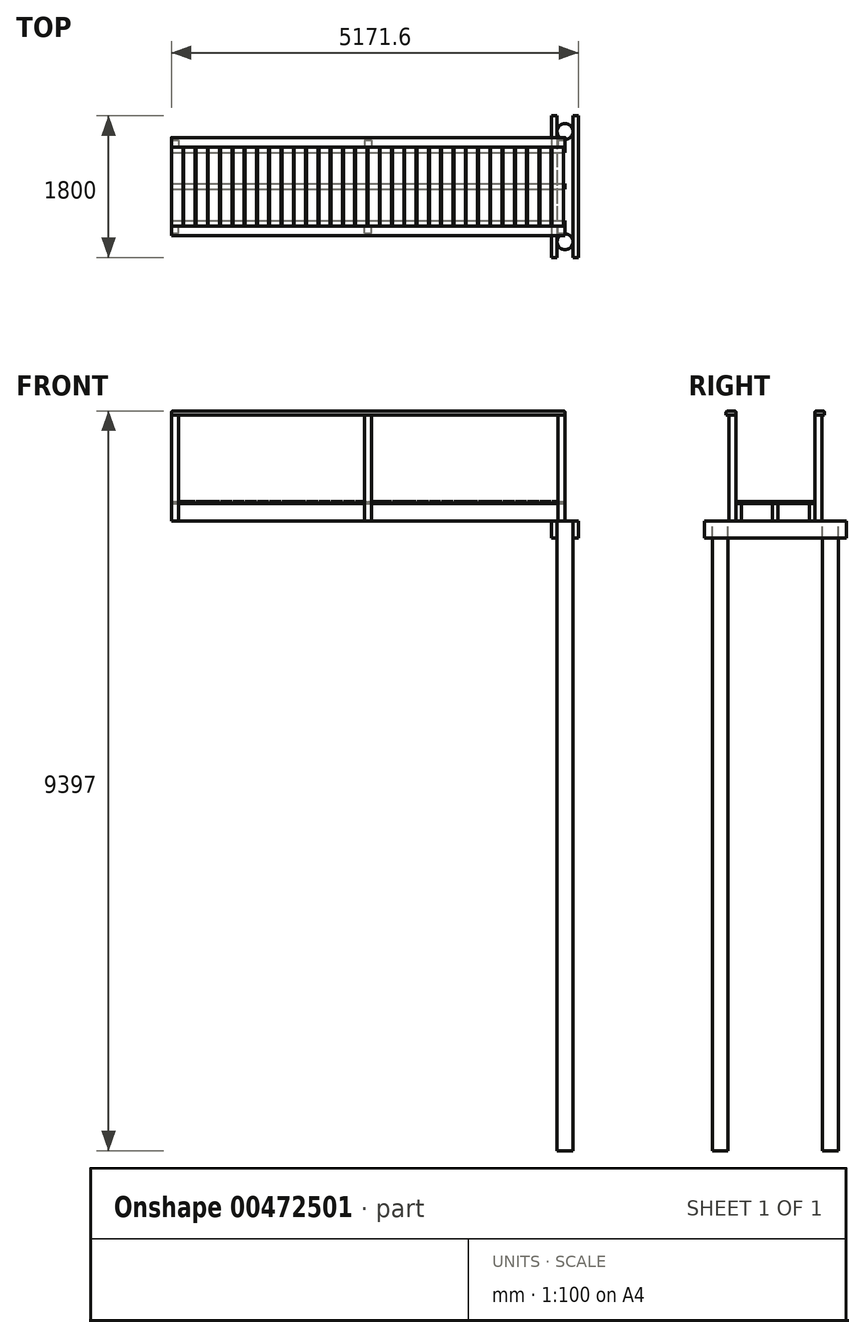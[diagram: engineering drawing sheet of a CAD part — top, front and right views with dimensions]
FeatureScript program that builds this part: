
annotation { "Feature Type Name" : "Feature", "Feature Type Description" : "" }
export const myFeature = defineFeature(function(context is Context, id is Id, definition is map)
    precondition{}
    {
        {
            var Q0;
            Q0=qCreatedBy(makeId("Top.planeOp"),FACE);
            var sketch = newSketch(context, id + "F0", { "sketchPlane" : qUnion([Q0])});
            skCircle(sketch, "E0", {"center": v(-387.32, 554.23) * mm, "radius": 100 * mm});
            skCircle(sketch, "E1", {"center": v(-387.32, -845.77) * mm, "radius": 100 * mm});
            skSolve(sketch);
        }
        {
            var Q0;
            Q0=qCreatedBy(makeId("Top.planeOp"),FACE);
            var sketch = newSketch(context, id + "F1", { "sketchPlane" : qUnion([Q0])});
            skLineSegment(sketch, "E2.bottom", {"start": v(-557.32, 754.23) * mm, "end": v(-487.32, 754.23) * mm});
            skLineSegment(sketch, "E2.top", {"start": v(-557.32, -1045.77) * mm, "end": v(-487.32, -1045.77) * mm});
            skLineSegment(sketch, "E2.left", {"start": v(-557.32, 754.23) * mm, "end": v(-557.32, -1045.77) * mm});
            skLineSegment(sketch, "E2.right", {"start": v(-487.32, 754.23) * mm, "end": v(-487.32, -1045.77) * mm});
            skLineSegment(sketch, "E3.left", {"start": v(-557.32, 754.23) * mm, "end": v(-557.32, 754.23) * mm});
            skLineSegment(sketch, "E3.right", {"start": v(-487.32, 754.23) * mm, "end": v(-487.32, 754.23) * mm});
            skLineSegment(sketch, "E4.MirrorCS", {"start": v(-285.72, 754.23) * mm, "end": v(-285.72, -1045.77) * mm});
            skLineSegment(sketch, "E5.MirrorCS", {"start": v(-215.72, 754.23) * mm, "end": v(-215.72, -1045.77) * mm});
            skLineSegment(sketch, "E6.MirrorCS", {"start": v(-215.72, 754.23) * mm, "end": v(-285.72, 754.23) * mm});
            skLineSegment(sketch, "E7.MirrorCS", {"start": v(-215.72, -1045.77) * mm, "end": v(-285.72, -1045.77) * mm});
            skSolve(sketch);
        }
        {
            var Q0;
            Q0 = qSketchRegion(id + "F0", true);
            extrude(context, id + "F2", {"entities" : qUnion([Q0]), "oppositeDirection" : true, "depth" : 8000 * mm});
        }
        {
            var Q0;
            Q0 = qSketchRegion(id + "F1", true);
            extrude(context, id + "F3", {"entities" : qUnion([Q0]), "oppositeDirection" : true, "depth" : 220 * mm});
        }
        {
            var Q0;
            Q0=qCreatedBy(makeId("Top.planeOp"),FACE);
            var sketch = newSketch(context, id + "F4", { "sketchPlane" : qUnion([Q0])});
            skLineSegment(sketch, "E8.bottom", {"start": v(-5387.32, 354.23) * mm, "end": v(-387.32, 354.23) * mm});
            skLineSegment(sketch, "E8.top", {"start": v(-5387.32, 284.23) * mm, "end": v(-387.32, 284.23) * mm});
            skLineSegment(sketch, "E8.left", {"start": v(-5387.32, 354.23) * mm, "end": v(-5387.32, 284.23) * mm});
            skLineSegment(sketch, "E8.right", {"start": v(-387.32, 354.23) * mm, "end": v(-387.32, 284.23) * mm});
            skLineSegment(sketch, "E9.0.1.0", {"start": v(-5387.32, -110.77) * mm, "end": v(-387.32, -110.77) * mm});
            skLineSegment(sketch, "E9.0.1.1", {"start": v(-5387.32, -180.77) * mm, "end": v(-387.32, -180.77) * mm});
            skLineSegment(sketch, "E9.0.1.2", {"start": v(-387.32, -110.77) * mm, "end": v(-387.32, -180.77) * mm});
            skLineSegment(sketch, "E9.0.1.3", {"start": v(-5387.32, -110.77) * mm, "end": v(-5387.32, -180.77) * mm});
            skLineSegment(sketch, "E9.0.2.0", {"start": v(-5387.32, -575.77) * mm, "end": v(-387.32, -575.77) * mm});
            skLineSegment(sketch, "E9.0.2.1", {"start": v(-5387.32, -645.77) * mm, "end": v(-387.32, -645.77) * mm});
            skLineSegment(sketch, "E9.0.2.2", {"start": v(-387.32, -575.77) * mm, "end": v(-387.32, -645.77) * mm});
            skLineSegment(sketch, "E9.0.2.3", {"start": v(-5387.32, -575.77) * mm, "end": v(-5387.32, -645.77) * mm});
            skLineSegment(sketch, "E9.direction1", {"start": v(-5387.32, 354.23) * mm, "end": v(-5387.32, 354.23) * mm});
            skLineSegment(sketch, "E9.direction2", {"start": v(-5387.32, 354.23) * mm, "end": v(-5387.32, -110.77) * mm, "construction": true});
            skSolve(sketch);
        }
        {
            var Q0;
            Q0=makeQuery(id+"F4.imprint","IMPRINT",FACE,{"disambiguationData":[TD([[makeQuery(id+"F4.imprint","IMPRINT",EDGE,{"derivedFrom":sQuery(id+"F4.wireOp",EDGE,"E8.bottom")}),-1.0]])]});
            var Q1;
            Q1=makeQuery(id+"F4.imprint","IMPRINT",FACE,{"disambiguationData":[TD([[makeQuery(id+"F4.imprint","IMPRINT",EDGE,{"derivedFrom":sQuery(id+"F4.wireOp",EDGE,"E9.0.2.0")}),-1.0]])]});
            var Q2;
            Q2=makeQuery(id+"F4.imprint","IMPRINT",FACE,{"disambiguationData":[TD([[makeQuery(id+"F4.imprint","IMPRINT",EDGE,{"derivedFrom":sQuery(id+"F4.wireOp",EDGE,"E9.0.1.0")}),-1.0]])]});
            extrude(context, id + "F5", {"entities" : qUnion([Q0, Q1, Q2]), "depth" : 220 * mm});
        }
        {
            var Q0;
            Q0=makeQuery(id+"F5.opExtrude","CAP_FACE",FACE,{"disambiguationData":[OSD([sQuery(id+"F4.wireOp",EDGE,"E8.bottom"),sQuery(id+"F4.wireOp",EDGE,"E8.top"),sQuery(id+"F4.wireOp",EDGE,"E8.left"),sQuery(id+"F4.wireOp",EDGE,"E8.right")])],"isStart":false});
            var sketch = newSketch(context, id + "F6", { "sketchPlane" : qUnion([Q0])});
            skLineSegment(sketch, "E10.bottom", {"start": v(-5387.32, 354.23) * mm, "end": v(-5242.32, 354.23) * mm});
            skLineSegment(sketch, "E10.top", {"start": v(-5387.32, -645.77) * mm, "end": v(-5242.32, -645.77) * mm});
            skLineSegment(sketch, "E10.left", {"start": v(-5387.32, 354.23) * mm, "end": v(-5387.32, -645.77) * mm});
            skLineSegment(sketch, "E10.right", {"start": v(-5242.32, 354.23) * mm, "end": v(-5242.32, -645.77) * mm});
            skLineSegment(sketch, "E11.1.0.0", {"start": v(-5086.32, 354.23) * mm, "end": v(-5086.32, -645.77) * mm});
            skLineSegment(sketch, "E11.1.0.1", {"start": v(-5231.32, 354.23) * mm, "end": v(-5086.32, 354.23) * mm});
            skLineSegment(sketch, "E11.1.0.2", {"start": v(-5231.32, 354.23) * mm, "end": v(-5231.32, -645.77) * mm});
            skLineSegment(sketch, "E11.1.0.3", {"start": v(-5231.32, -645.77) * mm, "end": v(-5086.32, -645.77) * mm});
            skLineSegment(sketch, "E11.2.0.0", {"start": v(-4930.32, 354.23) * mm, "end": v(-4930.32, -645.77) * mm});
            skLineSegment(sketch, "E11.2.0.1", {"start": v(-5075.32, 354.23) * mm, "end": v(-4930.32, 354.23) * mm});
            skLineSegment(sketch, "E11.2.0.2", {"start": v(-5075.32, 354.23) * mm, "end": v(-5075.32, -645.77) * mm});
            skLineSegment(sketch, "E11.2.0.3", {"start": v(-5075.32, -645.77) * mm, "end": v(-4930.32, -645.77) * mm});
            skLineSegment(sketch, "E11.3.0.0", {"start": v(-4774.32, 354.23) * mm, "end": v(-4774.32, -645.77) * mm});
            skLineSegment(sketch, "E11.3.0.1", {"start": v(-4919.32, 354.23) * mm, "end": v(-4774.32, 354.23) * mm});
            skLineSegment(sketch, "E11.3.0.2", {"start": v(-4919.32, 354.23) * mm, "end": v(-4919.32, -645.77) * mm});
            skLineSegment(sketch, "E11.3.0.3", {"start": v(-4919.32, -645.77) * mm, "end": v(-4774.32, -645.77) * mm});
            skLineSegment(sketch, "E11.4.0.0", {"start": v(-4618.32, 354.23) * mm, "end": v(-4618.32, -645.77) * mm});
            skLineSegment(sketch, "E11.4.0.1", {"start": v(-4763.32, 354.23) * mm, "end": v(-4618.32, 354.23) * mm});
            skLineSegment(sketch, "E11.4.0.2", {"start": v(-4763.32, 354.23) * mm, "end": v(-4763.32, -645.77) * mm});
            skLineSegment(sketch, "E11.4.0.3", {"start": v(-4763.32, -645.77) * mm, "end": v(-4618.32, -645.77) * mm});
            skLineSegment(sketch, "E11.5.0.0", {"start": v(-4462.32, 354.23) * mm, "end": v(-4462.32, -645.77) * mm});
            skLineSegment(sketch, "E11.5.0.1", {"start": v(-4607.32, 354.23) * mm, "end": v(-4462.32, 354.23) * mm});
            skLineSegment(sketch, "E11.5.0.2", {"start": v(-4607.32, 354.23) * mm, "end": v(-4607.32, -645.77) * mm});
            skLineSegment(sketch, "E11.5.0.3", {"start": v(-4607.32, -645.77) * mm, "end": v(-4462.32, -645.77) * mm});
            skLineSegment(sketch, "E11.6.0.0", {"start": v(-4306.32, 354.23) * mm, "end": v(-4306.32, -645.77) * mm});
            skLineSegment(sketch, "E11.6.0.1", {"start": v(-4451.32, 354.23) * mm, "end": v(-4306.32, 354.23) * mm});
            skLineSegment(sketch, "E11.6.0.2", {"start": v(-4451.32, 354.23) * mm, "end": v(-4451.32, -645.77) * mm});
            skLineSegment(sketch, "E11.6.0.3", {"start": v(-4451.32, -645.77) * mm, "end": v(-4306.32, -645.77) * mm});
            skLineSegment(sketch, "E11.7.0.0", {"start": v(-4150.32, 354.23) * mm, "end": v(-4150.32, -645.77) * mm});
            skLineSegment(sketch, "E11.7.0.1", {"start": v(-4295.32, 354.23) * mm, "end": v(-4150.32, 354.23) * mm});
            skLineSegment(sketch, "E11.7.0.2", {"start": v(-4295.32, 354.23) * mm, "end": v(-4295.32, -645.77) * mm});
            skLineSegment(sketch, "E11.7.0.3", {"start": v(-4295.32, -645.77) * mm, "end": v(-4150.32, -645.77) * mm});
            skLineSegment(sketch, "E11.8.0.0", {"start": v(-3994.32, 354.23) * mm, "end": v(-3994.32, -645.77) * mm});
            skLineSegment(sketch, "E11.8.0.1", {"start": v(-4139.32, 354.23) * mm, "end": v(-3994.32, 354.23) * mm});
            skLineSegment(sketch, "E11.8.0.2", {"start": v(-4139.32, 354.23) * mm, "end": v(-4139.32, -645.77) * mm});
            skLineSegment(sketch, "E11.8.0.3", {"start": v(-4139.32, -645.77) * mm, "end": v(-3994.32, -645.77) * mm});
            skLineSegment(sketch, "E11.9.0.0", {"start": v(-3838.32, 354.23) * mm, "end": v(-3838.32, -645.77) * mm});
            skLineSegment(sketch, "E11.9.0.1", {"start": v(-3983.32, 354.23) * mm, "end": v(-3838.32, 354.23) * mm});
            skLineSegment(sketch, "E11.9.0.2", {"start": v(-3983.32, 354.23) * mm, "end": v(-3983.32, -645.77) * mm});
            skLineSegment(sketch, "E11.9.0.3", {"start": v(-3983.32, -645.77) * mm, "end": v(-3838.32, -645.77) * mm});
            skLineSegment(sketch, "E11.10.0.0", {"start": v(-3682.32, 354.23) * mm, "end": v(-3682.32, -645.77) * mm});
            skLineSegment(sketch, "E11.10.0.1", {"start": v(-3827.32, 354.23) * mm, "end": v(-3682.32, 354.23) * mm});
            skLineSegment(sketch, "E11.10.0.2", {"start": v(-3827.32, 354.23) * mm, "end": v(-3827.32, -645.77) * mm});
            skLineSegment(sketch, "E11.10.0.3", {"start": v(-3827.32, -645.77) * mm, "end": v(-3682.32, -645.77) * mm});
            skLineSegment(sketch, "E11.11.0.0", {"start": v(-3526.32, 354.23) * mm, "end": v(-3526.32, -645.77) * mm});
            skLineSegment(sketch, "E11.11.0.1", {"start": v(-3671.32, 354.23) * mm, "end": v(-3526.32, 354.23) * mm});
            skLineSegment(sketch, "E11.11.0.2", {"start": v(-3671.32, 354.23) * mm, "end": v(-3671.32, -645.77) * mm});
            skLineSegment(sketch, "E11.11.0.3", {"start": v(-3671.32, -645.77) * mm, "end": v(-3526.32, -645.77) * mm});
            skLineSegment(sketch, "E11.12.0.0", {"start": v(-3370.32, 354.23) * mm, "end": v(-3370.32, -645.77) * mm});
            skLineSegment(sketch, "E11.12.0.1", {"start": v(-3515.32, 354.23) * mm, "end": v(-3370.32, 354.23) * mm});
            skLineSegment(sketch, "E11.12.0.2", {"start": v(-3515.32, 354.23) * mm, "end": v(-3515.32, -645.77) * mm});
            skLineSegment(sketch, "E11.12.0.3", {"start": v(-3515.32, -645.77) * mm, "end": v(-3370.32, -645.77) * mm});
            skLineSegment(sketch, "E11.13.0.0", {"start": v(-3214.32, 354.23) * mm, "end": v(-3214.32, -645.77) * mm});
            skLineSegment(sketch, "E11.13.0.1", {"start": v(-3359.32, 354.23) * mm, "end": v(-3214.32, 354.23) * mm});
            skLineSegment(sketch, "E11.13.0.2", {"start": v(-3359.32, 354.23) * mm, "end": v(-3359.32, -645.77) * mm});
            skLineSegment(sketch, "E11.13.0.3", {"start": v(-3359.32, -645.77) * mm, "end": v(-3214.32, -645.77) * mm});
            skLineSegment(sketch, "E11.14.0.0", {"start": v(-3058.32, 354.23) * mm, "end": v(-3058.32, -645.77) * mm});
            skLineSegment(sketch, "E11.14.0.1", {"start": v(-3203.32, 354.23) * mm, "end": v(-3058.32, 354.23) * mm});
            skLineSegment(sketch, "E11.14.0.2", {"start": v(-3203.32, 354.23) * mm, "end": v(-3203.32, -645.77) * mm});
            skLineSegment(sketch, "E11.14.0.3", {"start": v(-3203.32, -645.77) * mm, "end": v(-3058.32, -645.77) * mm});
            skLineSegment(sketch, "E11.15.0.0", {"start": v(-2902.32, 354.23) * mm, "end": v(-2902.32, -645.77) * mm});
            skLineSegment(sketch, "E11.15.0.1", {"start": v(-3047.32, 354.23) * mm, "end": v(-2902.32, 354.23) * mm});
            skLineSegment(sketch, "E11.15.0.2", {"start": v(-3047.32, 354.23) * mm, "end": v(-3047.32, -645.77) * mm});
            skLineSegment(sketch, "E11.15.0.3", {"start": v(-3047.32, -645.77) * mm, "end": v(-2902.32, -645.77) * mm});
            skLineSegment(sketch, "E11.16.0.0", {"start": v(-2746.32, 354.23) * mm, "end": v(-2746.32, -645.77) * mm});
            skLineSegment(sketch, "E11.16.0.1", {"start": v(-2891.32, 354.23) * mm, "end": v(-2746.32, 354.23) * mm});
            skLineSegment(sketch, "E11.16.0.2", {"start": v(-2891.32, 354.23) * mm, "end": v(-2891.32, -645.77) * mm});
            skLineSegment(sketch, "E11.16.0.3", {"start": v(-2891.32, -645.77) * mm, "end": v(-2746.32, -645.77) * mm});
            skLineSegment(sketch, "E11.17.0.0", {"start": v(-2590.32, 354.23) * mm, "end": v(-2590.32, -645.77) * mm});
            skLineSegment(sketch, "E11.17.0.1", {"start": v(-2735.32, 354.23) * mm, "end": v(-2590.32, 354.23) * mm});
            skLineSegment(sketch, "E11.17.0.2", {"start": v(-2735.32, 354.23) * mm, "end": v(-2735.32, -645.77) * mm});
            skLineSegment(sketch, "E11.17.0.3", {"start": v(-2735.32, -645.77) * mm, "end": v(-2590.32, -645.77) * mm});
            skLineSegment(sketch, "E11.18.0.0", {"start": v(-2434.32, 354.23) * mm, "end": v(-2434.32, -645.77) * mm});
            skLineSegment(sketch, "E11.18.0.1", {"start": v(-2579.32, 354.23) * mm, "end": v(-2434.32, 354.23) * mm});
            skLineSegment(sketch, "E11.18.0.2", {"start": v(-2579.32, 354.23) * mm, "end": v(-2579.32, -645.77) * mm});
            skLineSegment(sketch, "E11.18.0.3", {"start": v(-2579.32, -645.77) * mm, "end": v(-2434.32, -645.77) * mm});
            skLineSegment(sketch, "E11.19.0.0", {"start": v(-2278.32, 354.23) * mm, "end": v(-2278.32, -645.77) * mm});
            skLineSegment(sketch, "E11.19.0.1", {"start": v(-2423.32, 354.23) * mm, "end": v(-2278.32, 354.23) * mm});
            skLineSegment(sketch, "E11.19.0.2", {"start": v(-2423.32, 354.23) * mm, "end": v(-2423.32, -645.77) * mm});
            skLineSegment(sketch, "E11.19.0.3", {"start": v(-2423.32, -645.77) * mm, "end": v(-2278.32, -645.77) * mm});
            skLineSegment(sketch, "E11.20.0.0", {"start": v(-2122.32, 354.23) * mm, "end": v(-2122.32, -645.77) * mm});
            skLineSegment(sketch, "E11.20.0.1", {"start": v(-2267.32, 354.23) * mm, "end": v(-2122.32, 354.23) * mm});
            skLineSegment(sketch, "E11.20.0.2", {"start": v(-2267.32, 354.23) * mm, "end": v(-2267.32, -645.77) * mm});
            skLineSegment(sketch, "E11.20.0.3", {"start": v(-2267.32, -645.77) * mm, "end": v(-2122.32, -645.77) * mm});
            skLineSegment(sketch, "E11.21.0.0", {"start": v(-1966.32, 354.23) * mm, "end": v(-1966.32, -645.77) * mm});
            skLineSegment(sketch, "E11.21.0.1", {"start": v(-2111.32, 354.23) * mm, "end": v(-1966.32, 354.23) * mm});
            skLineSegment(sketch, "E11.21.0.2", {"start": v(-2111.32, 354.23) * mm, "end": v(-2111.32, -645.77) * mm});
            skLineSegment(sketch, "E11.21.0.3", {"start": v(-2111.32, -645.77) * mm, "end": v(-1966.32, -645.77) * mm});
            skLineSegment(sketch, "E11.22.0.0", {"start": v(-1810.32, 354.23) * mm, "end": v(-1810.32, -645.77) * mm});
            skLineSegment(sketch, "E11.22.0.1", {"start": v(-1955.32, 354.23) * mm, "end": v(-1810.32, 354.23) * mm});
            skLineSegment(sketch, "E11.22.0.2", {"start": v(-1955.32, 354.23) * mm, "end": v(-1955.32, -645.77) * mm});
            skLineSegment(sketch, "E11.22.0.3", {"start": v(-1955.32, -645.77) * mm, "end": v(-1810.32, -645.77) * mm});
            skLineSegment(sketch, "E11.23.0.0", {"start": v(-1654.32, 354.23) * mm, "end": v(-1654.32, -645.77) * mm});
            skLineSegment(sketch, "E11.23.0.1", {"start": v(-1799.32, 354.23) * mm, "end": v(-1654.32, 354.23) * mm});
            skLineSegment(sketch, "E11.23.0.2", {"start": v(-1799.32, 354.23) * mm, "end": v(-1799.32, -645.77) * mm});
            skLineSegment(sketch, "E11.23.0.3", {"start": v(-1799.32, -645.77) * mm, "end": v(-1654.32, -645.77) * mm});
            skLineSegment(sketch, "E11.24.0.0", {"start": v(-1498.32, 354.23) * mm, "end": v(-1498.32, -645.77) * mm});
            skLineSegment(sketch, "E11.24.0.1", {"start": v(-1643.32, 354.23) * mm, "end": v(-1498.32, 354.23) * mm});
            skLineSegment(sketch, "E11.24.0.2", {"start": v(-1643.32, 354.23) * mm, "end": v(-1643.32, -645.77) * mm});
            skLineSegment(sketch, "E11.24.0.3", {"start": v(-1643.32, -645.77) * mm, "end": v(-1498.32, -645.77) * mm});
            skLineSegment(sketch, "E11.25.0.0", {"start": v(-1342.32, 354.23) * mm, "end": v(-1342.32, -645.77) * mm});
            skLineSegment(sketch, "E11.25.0.1", {"start": v(-1487.32, 354.23) * mm, "end": v(-1342.32, 354.23) * mm});
            skLineSegment(sketch, "E11.25.0.2", {"start": v(-1487.32, 354.23) * mm, "end": v(-1487.32, -645.77) * mm});
            skLineSegment(sketch, "E11.25.0.3", {"start": v(-1487.32, -645.77) * mm, "end": v(-1342.32, -645.77) * mm});
            skLineSegment(sketch, "E11.26.0.0", {"start": v(-1186.32, 354.23) * mm, "end": v(-1186.32, -645.77) * mm});
            skLineSegment(sketch, "E11.26.0.1", {"start": v(-1331.32, 354.23) * mm, "end": v(-1186.32, 354.23) * mm});
            skLineSegment(sketch, "E11.26.0.2", {"start": v(-1331.32, 354.23) * mm, "end": v(-1331.32, -645.77) * mm});
            skLineSegment(sketch, "E11.26.0.3", {"start": v(-1331.32, -645.77) * mm, "end": v(-1186.32, -645.77) * mm});
            skLineSegment(sketch, "E11.27.0.0", {"start": v(-1030.32, 354.23) * mm, "end": v(-1030.32, -645.77) * mm});
            skLineSegment(sketch, "E11.27.0.1", {"start": v(-1175.32, 354.23) * mm, "end": v(-1030.32, 354.23) * mm});
            skLineSegment(sketch, "E11.27.0.2", {"start": v(-1175.32, 354.23) * mm, "end": v(-1175.32, -645.77) * mm});
            skLineSegment(sketch, "E11.27.0.3", {"start": v(-1175.32, -645.77) * mm, "end": v(-1030.32, -645.77) * mm});
            skLineSegment(sketch, "E11.28.0.0", {"start": v(-874.32, 354.23) * mm, "end": v(-874.32, -645.77) * mm});
            skLineSegment(sketch, "E11.28.0.1", {"start": v(-1019.32, 354.23) * mm, "end": v(-874.32, 354.23) * mm});
            skLineSegment(sketch, "E11.28.0.2", {"start": v(-1019.32, 354.23) * mm, "end": v(-1019.32, -645.77) * mm});
            skLineSegment(sketch, "E11.28.0.3", {"start": v(-1019.32, -645.77) * mm, "end": v(-874.32, -645.77) * mm});
            skLineSegment(sketch, "E11.29.0.0", {"start": v(-718.32, 354.23) * mm, "end": v(-718.32, -645.77) * mm});
            skLineSegment(sketch, "E11.29.0.1", {"start": v(-863.32, 354.23) * mm, "end": v(-718.32, 354.23) * mm});
            skLineSegment(sketch, "E11.29.0.2", {"start": v(-863.32, 354.23) * mm, "end": v(-863.32, -645.77) * mm});
            skLineSegment(sketch, "E11.29.0.3", {"start": v(-863.32, -645.77) * mm, "end": v(-718.32, -645.77) * mm});
            skLineSegment(sketch, "E11.30.0.0", {"start": v(-562.32, 354.23) * mm, "end": v(-562.32, -645.77) * mm});
            skLineSegment(sketch, "E11.30.0.1", {"start": v(-707.32, 354.23) * mm, "end": v(-562.32, 354.23) * mm});
            skLineSegment(sketch, "E11.30.0.2", {"start": v(-707.32, 354.23) * mm, "end": v(-707.32, -645.77) * mm});
            skLineSegment(sketch, "E11.30.0.3", {"start": v(-707.32, -645.77) * mm, "end": v(-562.32, -645.77) * mm});
            skLineSegment(sketch, "E11.31.0.0", {"start": v(-406.32, 354.23) * mm, "end": v(-406.32, -645.77) * mm});
            skLineSegment(sketch, "E11.31.0.1", {"start": v(-551.32, 354.23) * mm, "end": v(-406.32, 354.23) * mm});
            skLineSegment(sketch, "E11.31.0.2", {"start": v(-551.32, 354.23) * mm, "end": v(-551.32, -645.77) * mm});
            skLineSegment(sketch, "E11.31.0.3", {"start": v(-551.32, -645.77) * mm, "end": v(-406.32, -645.77) * mm});
            skLineSegment(sketch, "E11.direction1", {"start": v(-5242.32, -645.77) * mm, "end": v(-5086.32, -645.77) * mm, "construction": true});
            skSolve(sketch);
        }
        {
            var Q0;
            Q0 = qSketchRegion(id + "F6", true);
            extrude(context, id + "F7", {"entities" : qUnion([Q0]), "depth" : 27 * mm});
        }
        {
            var Q0;
            Q0=makeQuery(id+"F5.opExtrude","SWEPT_FACE",FACE,{"disambiguationData":[OSD([sQuery(id+"F4.wireOp",EDGE,"E9.0.2.1")])]});
            var sketch = newSketch(context, id + "F8", { "sketchPlane" : qUnion([Q0])});
            skLineSegment(sketch, "E12.bottom", {"start": v(-5387.32, 0) * mm, "end": v(-5297.32, 0) * mm});
            skLineSegment(sketch, "E12.top", {"start": v(-5387.32, 1347) * mm, "end": v(-5297.32, 1347) * mm});
            skLineSegment(sketch, "E12.left", {"start": v(-5387.32, 0) * mm, "end": v(-5387.32, 1347) * mm});
            skLineSegment(sketch, "E12.right", {"start": v(-5297.32, 0) * mm, "end": v(-5297.32, 1347) * mm});
            skLineSegment(sketch, "E13.bottom", {"start": v(-387.32, 0) * mm, "end": v(-477.32, 0) * mm});
            skLineSegment(sketch, "E13.top", {"start": v(-387.32, 1347) * mm, "end": v(-477.32, 1347) * mm});
            skLineSegment(sketch, "E13.left", {"start": v(-387.32, 0) * mm, "end": v(-387.32, 1347) * mm});
            skLineSegment(sketch, "E13.right", {"start": v(-477.32, 0) * mm, "end": v(-477.32, 1347) * mm});
            skLineSegment(sketch, "E14.bottom", {"start": v(-2932.32, 1347) * mm, "end": v(-2842.32, 1347) * mm});
            skLineSegment(sketch, "E14.top", {"start": v(-2932.32, 0) * mm, "end": v(-2842.32, 0) * mm});
            skLineSegment(sketch, "E14.left", {"start": v(-2842.32, 1347) * mm, "end": v(-2842.32, 0) * mm});
            skLineSegment(sketch, "E14.right", {"start": v(-2932.32, 1347) * mm, "end": v(-2932.32, 0) * mm});
            skSolve(sketch);
        }
        {
            var Q0;
            Q0 = qSketchRegion(id + "F8", true);
            extrude(context, id + "F9", {"entities" : qUnion([Q0]), "depth" : 90 * mm});
        }
        {
            var Q0;
            Q0=makeQuery(id+"F5.opExtrude","SWEPT_FACE",FACE,{"disambiguationData":[OSD([sQuery(id+"F4.wireOp",EDGE,"E8.bottom")])]});
            var sketch = newSketch(context, id + "F10", { "sketchPlane" : qUnion([Q0])});
            skLineSegment(sketch, "E15.bottom", {"start": v(5387.32, 0) * mm, "end": v(5297.32, 0) * mm});
            skLineSegment(sketch, "E15.top", {"start": v(5387.32, 1347) * mm, "end": v(5297.32, 1347) * mm});
            skLineSegment(sketch, "E15.left", {"start": v(5387.32, 0) * mm, "end": v(5387.32, 1347) * mm});
            skLineSegment(sketch, "E15.right", {"start": v(5297.32, 0) * mm, "end": v(5297.32, 1347) * mm});
            skLineSegment(sketch, "E16.1.0.0", {"start": v(2842.32, 0) * mm, "end": v(2842.32, 1347) * mm});
            skLineSegment(sketch, "E16.1.0.1", {"start": v(2932.32, 1347) * mm, "end": v(2842.32, 1347) * mm});
            skLineSegment(sketch, "E16.1.0.2", {"start": v(2932.32, 0) * mm, "end": v(2932.32, 1347) * mm});
            skLineSegment(sketch, "E16.1.0.3", {"start": v(2932.32, 0) * mm, "end": v(2842.32, 0) * mm});
            skLineSegment(sketch, "E16.2.0.0", {"start": v(387.32, 0) * mm, "end": v(387.32, 1347) * mm});
            skLineSegment(sketch, "E16.2.0.1", {"start": v(477.32, 1347) * mm, "end": v(387.32, 1347) * mm});
            skLineSegment(sketch, "E16.2.0.2", {"start": v(477.32, 0) * mm, "end": v(477.32, 1347) * mm});
            skLineSegment(sketch, "E16.2.0.3", {"start": v(477.32, 0) * mm, "end": v(387.32, 0) * mm});
            skLineSegment(sketch, "E16.direction1", {"start": v(5297.32, 0) * mm, "end": v(2842.32, 0) * mm, "construction": true});
            skSolve(sketch);
        }
        {
            var Q0;
            Q0 = qSketchRegion(id + "F10", true);
            extrude(context, id + "F11", {"entities" : qUnion([Q0]), "depth" : 90 * mm});
        }
        {
            var Q0;
            Q0=makeQuery(id+"F11.opExtrude","SWEPT_FACE",FACE,{"disambiguationData":[OSD([sQuery(id+"F10.wireOp",EDGE,"E15.top")])]});
            var sketch = newSketch(context, id + "F12", { "sketchPlane" : qUnion([Q0])});
            skLineSegment(sketch, "E17.bottom", {"start": v(-5387.32, 479.23) * mm, "end": v(-387.32, 479.23) * mm});
            skLineSegment(sketch, "E17.top", {"start": v(-5387.32, 354.23) * mm, "end": v(-387.32, 354.23) * mm});
            skLineSegment(sketch, "E17.left", {"start": v(-5387.32, 479.23) * mm, "end": v(-5387.32, 354.23) * mm});
            skLineSegment(sketch, "E17.right", {"start": v(-387.32, 479.23) * mm, "end": v(-387.32, 354.23) * mm});
            skLineSegment(sketch, "E18.MirrorCS", {"start": v(-5387.32, -770.77) * mm, "end": v(-387.32, -770.77) * mm});
            skLineSegment(sketch, "E19.MirrorCS", {"start": v(-5387.32, -645.77) * mm, "end": v(-387.32, -645.77) * mm});
            skLineSegment(sketch, "E20.MirrorCS", {"start": v(-5387.32, -770.77) * mm, "end": v(-5387.32, -645.77) * mm});
            skLineSegment(sketch, "E21.MirrorCS", {"start": v(-387.32, -770.77) * mm, "end": v(-387.32, -645.77) * mm});
            skSolve(sketch);
        }
        {
            var Q0;
            Q0 = qSketchRegion(id + "F12", true);
            extrude(context, id + "F13", {"entities" : qUnion([Q0]), "depth" : 50 * mm});
        }
        {
            var Q0;
            Q0=makeQuery(id+"F13.opExtrude","CAP_EDGE",EDGE,{"disambiguationData":[OSD([sQuery(id+"F12.wireOp",EDGE,"E17.bottom")])],"isStart":false});
            var Q1;
            Q1=makeQuery(id+"F13.opExtrude","CAP_EDGE",EDGE,{"disambiguationData":[OSD([sQuery(id+"F12.wireOp",EDGE,"E18.MirrorCS")])],"isStart":false});
            var Q2;
            Q2=makeQuery(id+"F13.opExtrude","CAP_EDGE",EDGE,{"disambiguationData":[OSD([sQuery(id+"F12.wireOp",EDGE,"E20.MirrorCS")])],"isStart":false});
            var Q3;
            Q3=makeQuery(id+"F13.opExtrude","CAP_EDGE",EDGE,{"disambiguationData":[OSD([sQuery(id+"F12.wireOp",EDGE,"E17.top")])],"isStart":false});
            var Q4;
            Q4=makeQuery(id+"F13.opExtrude","CAP_EDGE",EDGE,{"disambiguationData":[OSD([sQuery(id+"F12.wireOp",EDGE,"E17.left")])],"isStart":false});
            var Q5;
            Q5=makeQuery(id+"F13.opExtrude","CAP_EDGE",EDGE,{"disambiguationData":[OSD([sQuery(id+"F12.wireOp",EDGE,"E17.right")])],"isStart":false});
            var Q6;
            Q6=makeQuery(id+"F13.opExtrude","CAP_EDGE",EDGE,{"disambiguationData":[OSD([sQuery(id+"F12.wireOp",EDGE,"E19.MirrorCS")])],"isStart":false});
            var Q7;
            Q7=makeQuery(id+"F13.opExtrude","CAP_EDGE",EDGE,{"disambiguationData":[OSD([sQuery(id+"F12.wireOp",EDGE,"E21.MirrorCS")])],"isStart":false});
            fillet(context, id + "F14", {"entities" : qUnion([Q0, Q1, Q2, Q3, Q4, Q5, Q6, Q7]), "radius" : 20 * mm, "tangentPropagation" : true, "allowEdgeOverflow" : false});
        }
    });
